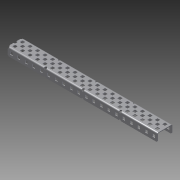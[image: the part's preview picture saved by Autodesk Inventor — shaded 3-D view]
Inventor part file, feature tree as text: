
AUTODESK INVENTOR PART (.ipt)
format: ipt  version: 2014 (Build 180170000, 170)  size: 1,506,816 bytes
history: native  units: in
note: dims shown in document units (in); Inventor stores cm internally (conversion verified against a paired STEP export)
features: other x1, imported_body x1, extrude x1, sketch x1
ambient origin geometry x8: Origin, YZ Plane, XZ Plane, XY Plane, X Axis, Y Axis, Z Axis, Center Point
bodies: Body1 (feature_tree)
feature tree (4):
  parser-record x1  (decoder bookkeeping rows leaked as tree rows — omitted from the tree; the rows remain in map.json)
  imported_body  "Base1"
  extrude  "Extrusion1"  [1 undecoded]
  sketch  "Sketch1"  dims[d0=1.0in d1=0.0in]
note: 1 required parameter value undecoded (feature->parameter linkage not recoverable at this tier; creation-order binding heuristic only, values carry confidence <= 0.55)
